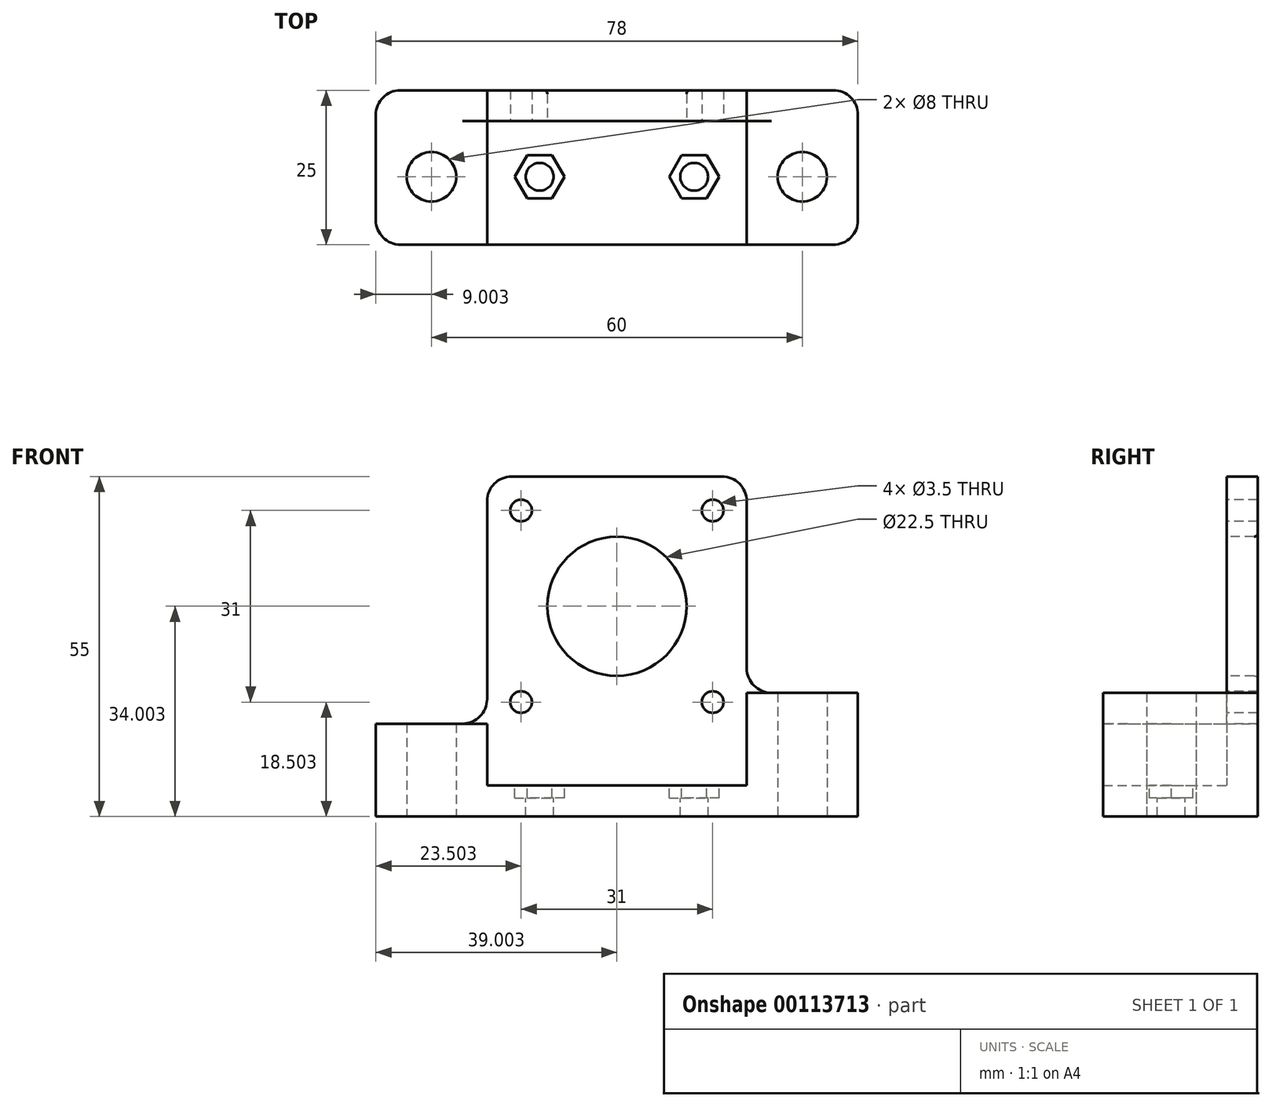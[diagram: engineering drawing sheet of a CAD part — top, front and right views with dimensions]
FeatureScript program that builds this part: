
annotation { "Feature Type Name" : "Feature", "Feature Type Description" : "" }
export const myFeature = defineFeature(function(context is Context, id is Id, definition is map)
    precondition{}
    {
        {
            var Q0;
            Q0=qCreatedBy(makeId("Front.planeOp"),FACE);
            var sketch = newSketch(context, id + "F0", { "sketchPlane" : qUnion([Q0])});
            skLineSegment(sketch, "E0", {"start": v(-49.77, -8.12) * mm, "end": v(-49.77, 6.88) * mm});
            skLineSegment(sketch, "E1", {"start": v(-49.77, 6.88) * mm, "end": v(-31.77, 6.88) * mm});
            skLineSegment(sketch, "E2", {"start": v(-31.77, 6.88) * mm, "end": v(-31.77, 46.88) * mm});
            skLineSegment(sketch, "E3", {"start": v(-31.77, 46.88) * mm, "end": v(10.23, 46.88) * mm});
            skLineSegment(sketch, "E4", {"start": v(10.23, 46.88) * mm, "end": v(10.23, 11.88) * mm});
            skLineSegment(sketch, "E5", {"start": v(10.23, 11.88) * mm, "end": v(28.23, 11.88) * mm});
            skLineSegment(sketch, "E6", {"start": v(28.23, 11.88) * mm, "end": v(28.23, -8.12) * mm});
            skLineSegment(sketch, "E7", {"start": v(28.23, -8.12) * mm, "end": v(-49.77, -8.12) * mm});
            skSolve(sketch);
        }
        {
            var Q0;
            Q0=makeQuery(id+"F0.imprint","IMPRINT",FACE,{"disambiguationData":[TD([[makeQuery(id+"F0.imprint","IMPRINT",EDGE,{"derivedFrom":sQuery(id+"F0.wireOp",EDGE,"E0")}),-1.0]])]});
            extrude(context, id + "F1", {"entities" : qUnion([Q0]), "depth" : 5 * mm});
        }
        {
            var Q0;
            Q0=makeQuery(id+"F1.opExtrude","CAP_FACE",FACE,{"disambiguationData":[OSD([sQuery(id+"F0.wireOp",EDGE,"E0"),sQuery(id+"F0.wireOp",EDGE,"E1"),sQuery(id+"F0.wireOp",EDGE,"E2"),sQuery(id+"F0.wireOp",EDGE,"E3"),sQuery(id+"F0.wireOp",EDGE,"E4"),sQuery(id+"F0.wireOp",EDGE,"E5"),sQuery(id+"F0.wireOp",EDGE,"E6"),sQuery(id+"F0.wireOp",EDGE,"E7")])],"isStart":false});
            var sketch = newSketch(context, id + "F2", { "sketchPlane" : qUnion([Q0])});
            skLineSegment(sketch, "E8.bottom", {"start": v(-31.77, 6.88) * mm, "end": v(-49.77, 6.88) * mm});
            skLineSegment(sketch, "E8.top", {"start": v(-31.77, -8.12) * mm, "end": v(-49.77, -8.12) * mm});
            skLineSegment(sketch, "E8.left", {"start": v(-31.77, 6.88) * mm, "end": v(-31.77, -8.12) * mm});
            skLineSegment(sketch, "E8.right", {"start": v(-49.77, 6.88) * mm, "end": v(-49.77, -8.12) * mm});
            skLineSegment(sketch, "E9.bottom", {"start": v(10.23, 11.88) * mm, "end": v(28.23, 11.88) * mm});
            skLineSegment(sketch, "E9.top", {"start": v(10.23, -8.12) * mm, "end": v(28.23, -8.12) * mm});
            skLineSegment(sketch, "E9.left", {"start": v(10.23, 11.88) * mm, "end": v(10.23, -8.12) * mm});
            skLineSegment(sketch, "E9.right", {"start": v(28.23, 11.88) * mm, "end": v(28.23, -8.12) * mm});
            skSolve(sketch);
        }
        {
            var Q0;
            Q0=makeQuery(id+"F2.imprint","IMPRINT",FACE,{"disambiguationData":[TD([[makeQuery(id+"F2.imprint","IMPRINT",EDGE,{"derivedFrom":sQuery(id+"F2.wireOp",EDGE,"E8.bottom")}),-1.0]])]});
            var Q1;
            Q1=makeQuery(id+"F2.imprint","IMPRINT",FACE,{"disambiguationData":[TD([[makeQuery(id+"F2.imprint","IMPRINT",EDGE,{"derivedFrom":sQuery(id+"F2.wireOp",EDGE,"E9.bottom")}),-1.0]])]});
            extrude(context, id + "F3", {"entities" : qUnion([Q0, Q1]), "operationType" : NewBodyOperationType.ADD, "depth" : 20 * mm});
        }
        {
            var Q0;
            Q0=makeQuery(id+"F3.boolean.opBoolean","MERGE",FACE,{"derivedFrom":[makeQuery(id+"F1.opExtrude","SWEPT_FACE",FACE,{"disambiguationData":[OSD([sQuery(id+"F0.wireOp",EDGE,"E7")])]}),makeQuery(id+"F3.opExtrude","SWEPT_FACE",FACE,{"disambiguationData":[OSD([sQuery(id+"F2.wireOp",EDGE,"E8.top")])]}),makeQuery(id+"F3.opExtrude","SWEPT_FACE",FACE,{"disambiguationData":[OSD([sQuery(id+"F2.wireOp",EDGE,"E9.top")])]})]});
            var sketch = newSketch(context, id + "F4", { "sketchPlane" : qUnion([Q0])});
            skCircle(sketch, "E10", {"center": v(-40.77, 14) * mm, "radius": 4 * mm});
            skCircle(sketch, "E11", {"center": v(19.23, 14) * mm, "radius": 4 * mm});
            skSolve(sketch);
        }
        {
            var Q0;
            Q0=makeQuery(id+"F4.imprint","IMPRINT",FACE,{"disambiguationData":[TD([[makeQuery(id+"F4.imprint","IMPRINT",EDGE,{"derivedFrom":sQuery(id+"F4.wireOp",EDGE,"E10")}),1.0]])]});
            var Q1;
            Q1=makeQuery(id+"F4.imprint","IMPRINT",FACE,{"disambiguationData":[TD([[makeQuery(id+"F4.imprint","IMPRINT",EDGE,{"derivedFrom":sQuery(id+"F4.wireOp",EDGE,"E11")}),1.0]])]});
            extrude(context, id + "F5", {"entities" : qUnion([Q0, Q1]), "operationType" : NewBodyOperationType.REMOVE, "oppositeDirection" : true, "depth" : 25 * mm});
        }
        {
            var Q0;
            Q0=makeQuery(id+"F1.opExtrude","CAP_FACE",FACE,{"disambiguationData":[OSD([sQuery(id+"F0.wireOp",EDGE,"E0"),sQuery(id+"F0.wireOp",EDGE,"E1"),sQuery(id+"F0.wireOp",EDGE,"E2"),sQuery(id+"F0.wireOp",EDGE,"E3"),sQuery(id+"F0.wireOp",EDGE,"E4"),sQuery(id+"F0.wireOp",EDGE,"E5"),sQuery(id+"F0.wireOp",EDGE,"E6"),sQuery(id+"F0.wireOp",EDGE,"E7")])],"isStart":false});
            var sketch = newSketch(context, id + "F6", { "sketchPlane" : qUnion([Q0])});
            skCircle(sketch, "E12", {"center": v(-10.77, 25.88) * mm, "radius": 11.25 * mm});
            skCircle(sketch, "E13", {"center": v(-26.27, 41.38) * mm, "radius": 1.75 * mm});
            skCircle(sketch, "E14.0.1.0", {"center": v(-26.27, 10.38) * mm, "radius": 1.75 * mm});
            skCircle(sketch, "E14.1.0.0", {"center": v(4.73, 41.38) * mm, "radius": 1.75 * mm});
            skCircle(sketch, "E14.1.1.0", {"center": v(4.73, 10.38) * mm, "radius": 1.75 * mm});
            skLineSegment(sketch, "E14.direction1", {"start": v(-26.27, 41.38) * mm, "end": v(4.73, 41.38) * mm, "construction": true});
            skLineSegment(sketch, "E14.direction2", {"start": v(-26.27, 41.38) * mm, "end": v(-26.27, 10.38) * mm, "construction": true});
            skSolve(sketch);
        }
        {
            var Q0;
            Q0=makeQuery(id+"F6.imprint","IMPRINT",FACE,{"disambiguationData":[TD([[makeQuery(id+"F6.imprint","IMPRINT",EDGE,{"derivedFrom":sQuery(id+"F6.wireOp",EDGE,"E13")}),1.0]])]});
            var Q1;
            Q1=makeQuery(id+"F6.imprint","IMPRINT",FACE,{"disambiguationData":[TD([[makeQuery(id+"F6.imprint","IMPRINT",EDGE,{"derivedFrom":sQuery(id+"F6.wireOp",EDGE,"E14.0.1.0")}),1.0]])]});
            var Q2;
            Q2=makeQuery(id+"F6.imprint","IMPRINT",FACE,{"disambiguationData":[TD([[makeQuery(id+"F6.imprint","IMPRINT",EDGE,{"derivedFrom":sQuery(id+"F6.wireOp",EDGE,"E12")}),1.0]])]});
            var Q3;
            Q3=makeQuery(id+"F6.imprint","IMPRINT",FACE,{"disambiguationData":[TD([[makeQuery(id+"F6.imprint","IMPRINT",EDGE,{"derivedFrom":sQuery(id+"F6.wireOp",EDGE,"E14.1.0.0")}),1.0]])]});
            var Q4;
            Q4=makeQuery(id+"F6.imprint","IMPRINT",FACE,{"disambiguationData":[TD([[makeQuery(id+"F6.imprint","IMPRINT",EDGE,{"derivedFrom":sQuery(id+"F6.wireOp",EDGE,"E14.1.1.0")}),1.0]])]});
            extrude(context, id + "F7", {"entities" : qUnion([Q0, Q1, Q2, Q3, Q4]), "operationType" : NewBodyOperationType.REMOVE, "oppositeDirection" : true, "depth" : 25 * mm});
        }
        {
            var Q0;
            Q0=makeQuery(id+"F1.opExtrude","CAP_FACE",FACE,{"disambiguationData":[OSD([sQuery(id+"F0.wireOp",EDGE,"E0"),sQuery(id+"F0.wireOp",EDGE,"E1"),sQuery(id+"F0.wireOp",EDGE,"E2"),sQuery(id+"F0.wireOp",EDGE,"E3"),sQuery(id+"F0.wireOp",EDGE,"E4"),sQuery(id+"F0.wireOp",EDGE,"E5"),sQuery(id+"F0.wireOp",EDGE,"E6"),sQuery(id+"F0.wireOp",EDGE,"E7")])],"isStart":false});
            var sketch = newSketch(context, id + "F8", { "sketchPlane" : qUnion([Q0])});
            skLineSegment(sketch, "E15.bottom", {"start": v(10.23, -8.12) * mm, "end": v(-31.77, -8.12) * mm});
            skLineSegment(sketch, "E15.top", {"start": v(10.23, -3.12) * mm, "end": v(-31.77, -3.12) * mm});
            skLineSegment(sketch, "E15.left", {"start": v(10.23, -8.12) * mm, "end": v(10.23, -3.12) * mm});
            skLineSegment(sketch, "E15.right", {"start": v(-31.77, -8.12) * mm, "end": v(-31.77, -3.12) * mm});
            skSolve(sketch);
        }
        {
            var Q0;
            Q0=makeQuery(id+"F8.imprint","IMPRINT",FACE,{"disambiguationData":[TD([[makeQuery(id+"F8.imprint","IMPRINT",EDGE,{"derivedFrom":sQuery(id+"F8.wireOp",EDGE,"E15.bottom")}),-1.0]])]});
            extrude(context, id + "F9", {"entities" : qUnion([Q0]), "operationType" : NewBodyOperationType.ADD, "depth" : 20 * mm});
        }
        {
            var Q0;
            Q0=makeQuery(id+"F9.opExtrude","SWEPT_FACE",FACE,{"disambiguationData":[OSD([sQuery(id+"F8.wireOp",EDGE,"E15.top")])]});
            var sketch = newSketch(context, id + "F10", { "sketchPlane" : qUnion([Q0])});
            skCircle(sketch, "E16", {"center": v(-23.27, -14) * mm, "radius": 2.25 * mm});
            skCircle(sketch, "E17", {"center": v(1.73, -14) * mm, "radius": 2.25 * mm});
            skCircle(sketch, "E18.cCircle", {"center": v(-23.27, -14) * mm, "radius": 3.5 * mm, "construction": true});
            skLineSegment(sketch, "E18.0", {"start": v(-19.23, -14) * mm, "end": v(-21.25, -17.5) * mm});
            skLineSegment(sketch, "E18.1", {"start": v(-21.25, -17.5) * mm, "end": v(-25.29, -17.5) * mm});
            skLineSegment(sketch, "E18.2", {"start": v(-25.29, -17.5) * mm, "end": v(-27.3, -14) * mm});
            skLineSegment(sketch, "E18.3", {"start": v(-27.3, -14) * mm, "end": v(-25.29, -10.5) * mm});
            skLineSegment(sketch, "E18.4", {"start": v(-25.29, -10.5) * mm, "end": v(-21.25, -10.5) * mm});
            skLineSegment(sketch, "E18.5", {"start": v(-21.25, -10.5) * mm, "end": v(-19.23, -14) * mm});
            skPoint(sketch, "E18.0.midPoint", {"position": v(-20.24, -15.75) * mm});
            skCircle(sketch, "E19.cCircle", {"center": v(1.73, -14) * mm, "radius": 3.5 * mm, "construction": true});
            skLineSegment(sketch, "E19.0", {"start": v(5.77, -14) * mm, "end": v(3.75, -17.5) * mm});
            skLineSegment(sketch, "E19.1", {"start": v(3.75, -17.5) * mm, "end": v(-0.29, -17.5) * mm});
            skLineSegment(sketch, "E19.2", {"start": v(-0.29, -17.5) * mm, "end": v(-2.3, -14) * mm});
            skLineSegment(sketch, "E19.3", {"start": v(-2.3, -14) * mm, "end": v(-0.29, -10.5) * mm});
            skLineSegment(sketch, "E19.4", {"start": v(-0.29, -10.5) * mm, "end": v(3.75, -10.5) * mm});
            skLineSegment(sketch, "E19.5", {"start": v(3.75, -10.5) * mm, "end": v(5.77, -14) * mm});
            skPoint(sketch, "E19.0.midPoint", {"position": v(4.76, -15.75) * mm});
            skSolve(sketch);
        }
        {
            var Q0;
            Q0=makeQuery(id+"F10.imprint","IMPRINT",FACE,{"disambiguationData":[TD([[makeQuery(id+"F10.imprint","IMPRINT",EDGE,{"derivedFrom":sQuery(id+"F10.wireOp",EDGE,"E16")}),1.0]])]});
            var Q1;
            Q1=makeQuery(id+"F10.imprint","IMPRINT",FACE,{"disambiguationData":[TD([[makeQuery(id+"F10.imprint","IMPRINT",EDGE,{"derivedFrom":sQuery(id+"F10.wireOp",EDGE,"E17")}),1.0]])]});
            extrude(context, id + "F11", {"entities" : qUnion([Q0, Q1]), "operationType" : NewBodyOperationType.REMOVE, "oppositeDirection" : true, "depth" : 25 * mm});
        }
        {
            var Q0;
            Q0=makeQuery(id+"F10.imprint","IMPRINT",FACE,{"disambiguationData":[TD([[makeQuery(id+"F10.imprint","IMPRINT",EDGE,{"derivedFrom":sQuery(id+"F10.wireOp",EDGE,"E16")}),-1.0]])]});
            var Q1;
            Q1=makeQuery(id+"F10.imprint","IMPRINT",FACE,{"disambiguationData":[TD([[makeQuery(id+"F10.imprint","IMPRINT",EDGE,{"derivedFrom":sQuery(id+"F10.wireOp",EDGE,"E17")}),-1.0]])]});
            extrude(context, id + "F12", {"entities" : qUnion([Q0, Q1]), "operationType" : NewBodyOperationType.REMOVE, "oppositeDirection" : true, "depth" : 2 * mm});
        }
        {
            var Q0;
            Q0=makeQuery(id+"F3.opExtrude","CAP_EDGE",EDGE,{"disambiguationData":[OSD([sQuery(id+"F2.wireOp",EDGE,"E8.right")])],"isStart":false});
            var Q1;
            Q1=makeQuery(id+"F3.opExtrude","CAP_EDGE",EDGE,{"disambiguationData":[OSD([sQuery(id+"F2.wireOp",EDGE,"E9.right")])],"isStart":false});
            var Q2;
            Q2=makeQuery(id+"F1.opExtrude","CAP_EDGE",EDGE,{"disambiguationData":[OSD([sQuery(id+"F0.wireOp",EDGE,"E6")])],"isStart":true});
            var Q3;
            Q3=makeQuery(id+"F1.opExtrude","CAP_EDGE",EDGE,{"disambiguationData":[OSD([sQuery(id+"F0.wireOp",EDGE,"E0")])],"isStart":true});
            var Q4;
            Q4=makeQuery(id+"F1.opExtrude","SWEPT_EDGE",EDGE,{"disambiguationData":[OSD([sQuery(id+"F0.wireOp",EDGE,"E2"),sQuery(id+"F0.wireOp",EDGE,"E3")])]});
            var Q5;
            Q5=makeQuery(id+"F1.opExtrude","SWEPT_EDGE",EDGE,{"disambiguationData":[OSD([sQuery(id+"F0.wireOp",EDGE,"E3"),sQuery(id+"F0.wireOp",EDGE,"E4")])]});
            var Q6;
            Q6=makeQuery(id+"F1.opExtrude","SWEPT_EDGE",EDGE,{"disambiguationData":[OSD([sQuery(id+"F0.wireOp",EDGE,"E1"),sQuery(id+"F0.wireOp",EDGE,"E2")])]});
            var Q7;
            Q7=makeQuery(id+"F1.opExtrude","SWEPT_EDGE",EDGE,{"disambiguationData":[OSD([sQuery(id+"F0.wireOp",EDGE,"E4"),sQuery(id+"F0.wireOp",EDGE,"E5")])]});
            fillet(context, id + "F13", {"entities" : qUnion([Q0, Q1, Q2, Q3, Q4, Q5, Q6, Q7]), "radius" : 4 * mm, "tangentPropagation" : true, "allowEdgeOverflow" : false});
        }
        {
            var Q0;
            Q0=makeQuery(id+"F7.boolean.opBoolean","INTERSECT",EDGE,{"derivedFrom":[makeQuery(id+"F1.opExtrude","CAP_FACE",FACE,{"disambiguationData":[OSD([sQuery(id+"F0.wireOp",EDGE,"E0"),sQuery(id+"F0.wireOp",EDGE,"E1"),sQuery(id+"F0.wireOp",EDGE,"E2"),sQuery(id+"F0.wireOp",EDGE,"E3"),sQuery(id+"F0.wireOp",EDGE,"E4"),sQuery(id+"F0.wireOp",EDGE,"E5"),sQuery(id+"F0.wireOp",EDGE,"E6"),sQuery(id+"F0.wireOp",EDGE,"E7")])],"isStart":true}),makeQuery(id+"F7.opExtrude","SWEPT_FACE",FACE,{"disambiguationData":[OSD([sQuery(id+"F6.wireOp",EDGE,"E12")])]})]});
            var Q1;
            Q1=makeQuery(id+"F7.boolean.opBoolean","COPY",EDGE,{"derivedFrom":makeQuery(id+"F7.opExtrude","CAP_EDGE",EDGE,{"disambiguationData":[OSD([sQuery(id+"F6.wireOp",EDGE,"E12")])],"isStart":true})});
            fillet(context, id + "F14", {"entities" : qUnion([Q0, Q1]), "radius" : 0.6 * mm, "tangentPropagation" : true, "allowEdgeOverflow" : false});
        }
    });
